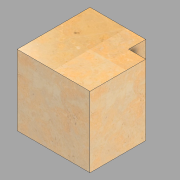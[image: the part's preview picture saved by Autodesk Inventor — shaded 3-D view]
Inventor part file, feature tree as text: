
AUTODESK INVENTOR PART (.ipt)
format: ipt  version: 2022.2 (Build 262287000, 287)  size: 139,264 bytes
history: native  units: in
note: dims shown in document units (in); Inventor stores cm internally (conversion verified against a paired STEP export)
features: extrude x2, sketch x2
ambient origin geometry x8: Origin, YZ Plane, XZ Plane, XY Plane, X Axis, Y Axis, Z Axis, Center Point
bodies: Solid1 (feature_tree)
feature tree (4):
  extrude  "Extrusion1"  Depth=8.0in
  extrude  "Extrusion2"  Depth=1.875in
  sketch  "Sketch1"  dims[d0=8.0in d1=8.0in]
  sketch  "Sketch2"  dims[d2=7.75in d3=0.0in d4=1.875in d5=1.875in d6=0.0in d7=0.0in]
